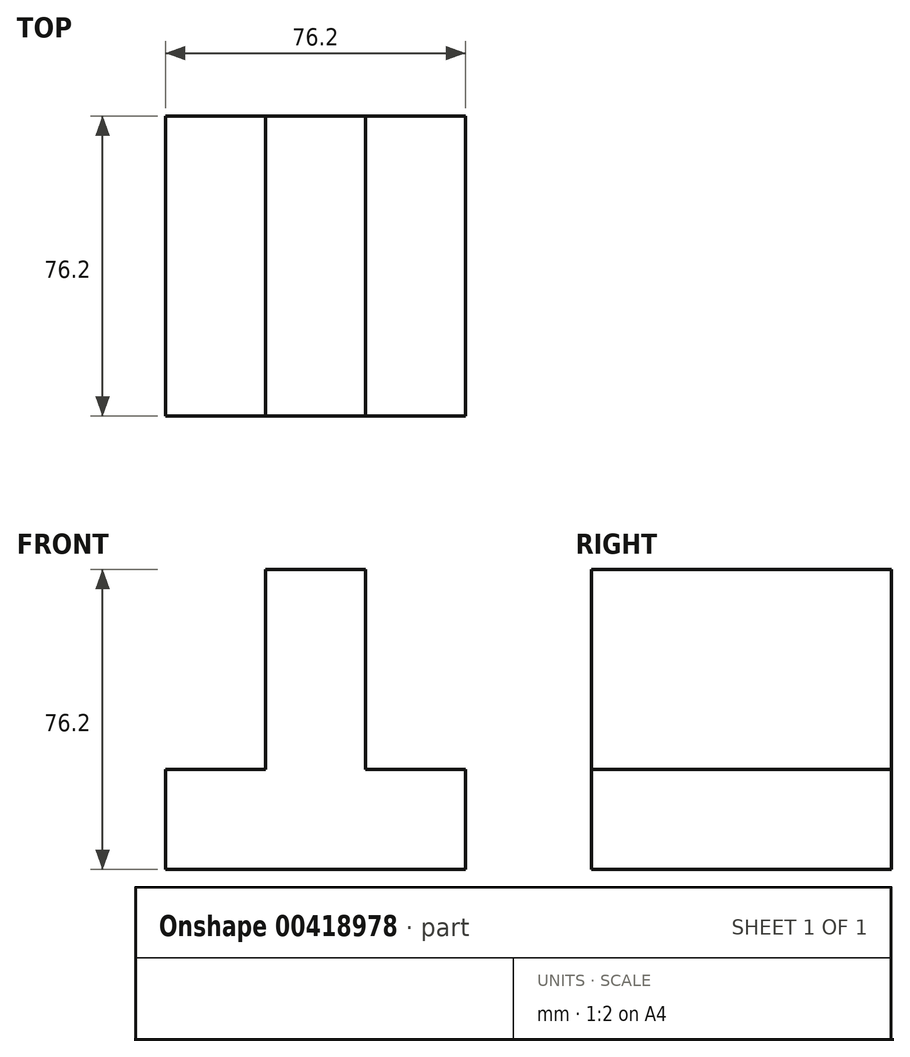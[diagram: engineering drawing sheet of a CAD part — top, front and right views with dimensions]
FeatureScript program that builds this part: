
annotation { "Feature Type Name" : "Feature", "Feature Type Description" : "" }
export const myFeature = defineFeature(function(context is Context, id is Id, definition is map)
    precondition{}
    {
        {
            var Q0;
            Q0=qCreatedBy(makeId("Front.planeOp"),FACE);
            var sketch = newSketch(context, id + "F0", { "sketchPlane" : qUnion([Q0])});
            skLineSegment(sketch, "E0", {"start": v(0, 0) * mm, "end": v(-76.2, 0) * mm});
            skLineSegment(sketch, "E1", {"start": v(0, 0) * mm, "end": v(0, 25.4) * mm});
            skLineSegment(sketch, "E2", {"start": v(0, 25.4) * mm, "end": v(-25.4, 25.4) * mm});
            skLineSegment(sketch, "E3", {"start": v(-25.4, 25.4) * mm, "end": v(-25.4, 76.2) * mm});
            skLineSegment(sketch, "E4", {"start": v(-25.4, 76.2) * mm, "end": v(-50.8, 76.2) * mm});
            skLineSegment(sketch, "E5", {"start": v(-50.8, 76.2) * mm, "end": v(-50.8, 25.4) * mm});
            skLineSegment(sketch, "E6", {"start": v(-50.8, 25.4) * mm, "end": v(-76.2, 25.4) * mm});
            skLineSegment(sketch, "E7", {"start": v(-76.2, 25.4) * mm, "end": v(-76.2, 0) * mm});
            skSolve(sketch);
        }
        {
            var Q0;
            Q0=makeQuery(id+"F0.imprint","IMPRINT",FACE,{"disambiguationData":[TD([[makeQuery(id+"F0.imprint","IMPRINT",EDGE,{"derivedFrom":sQuery(id+"F0.wireOp",EDGE,"E0")}),-1.0]])]});
            extrude(context, id + "F1", {"entities" : qUnion([Q0]), "depth" : 76.2 * mm});
        }
    });
